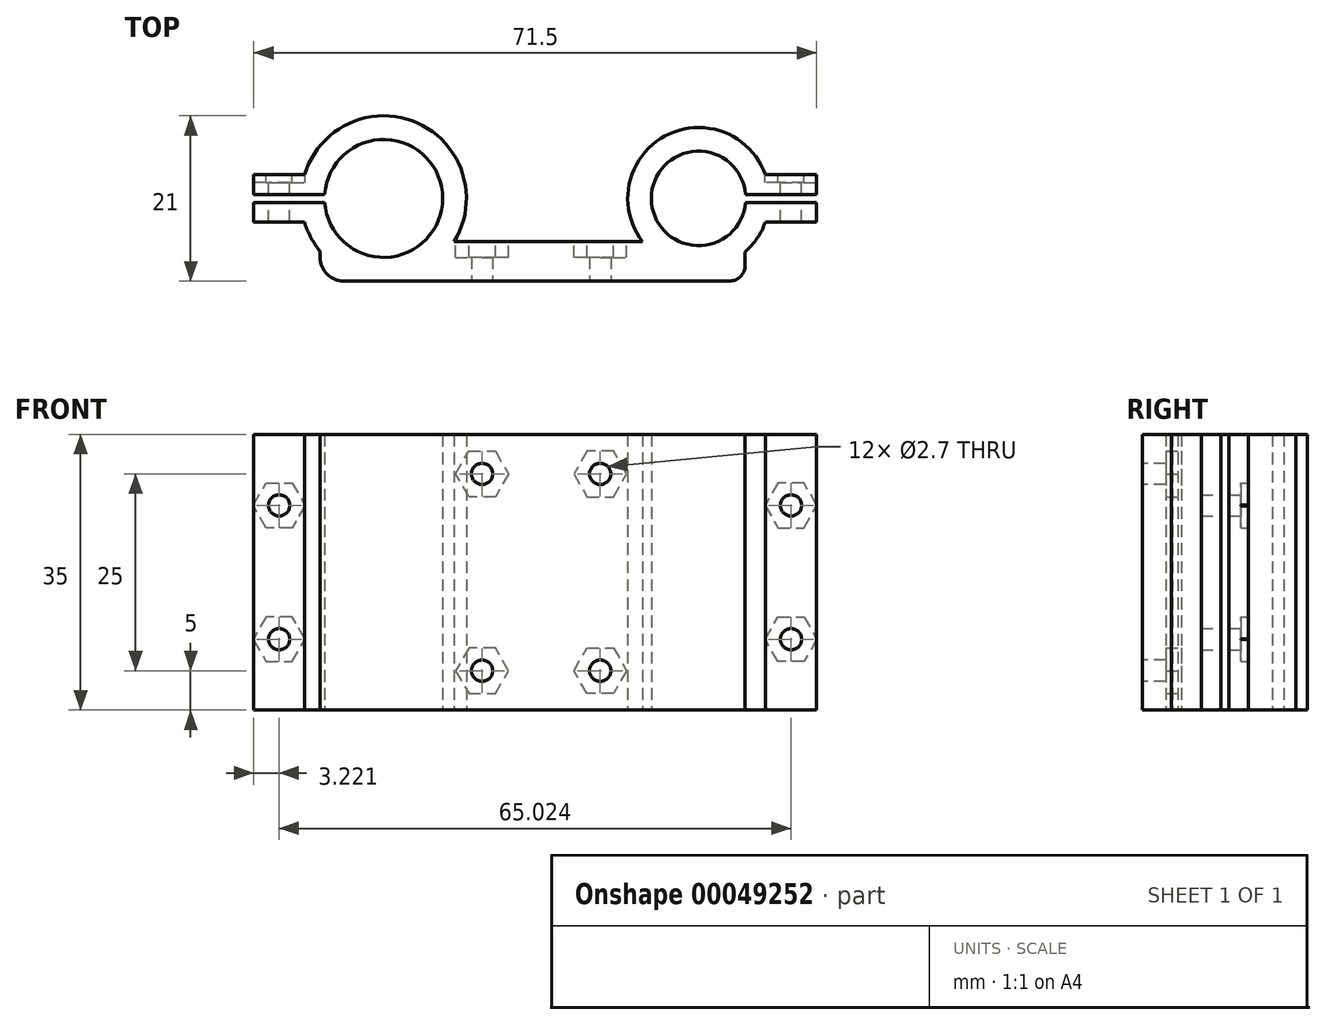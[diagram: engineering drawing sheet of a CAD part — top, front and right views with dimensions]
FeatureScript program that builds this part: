
annotation { "Feature Type Name" : "Feature", "Feature Type Description" : "" }
export const myFeature = defineFeature(function(context is Context, id is Id, definition is map)
    precondition{}
    {
        {
            var Q0;
            Q0=qCreatedBy(makeId("Top.planeOp"),FACE);
            var sketch = newSketch(context, id + "F0", { "sketchPlane" : qUnion([Q0])});
            skArc(sketch, "E0", {"start": v(-27.82, -25.7) * mm, "mid": v(-41.2, -21.15) * mm, "end": v(-42.53, -35.2) * mm});
            skArc(sketch, "E1", {"start": v(-30.33, -28.2) * mm, "mid": v(-42.3, -28.7) * mm, "end": v(-30.33, -29.2) * mm});
            skArc(sketch, "E2", {"start": v(-83.8, -29.2) * mm, "mid": v(-68.8, -28.7) * mm, "end": v(-83.8, -28.2) * mm});
            skArc(sketch, "E3", {"start": v(-86.37, -31.7) * mm, "mid": v(-85.57, -33.66) * mm, "end": v(-84.4, -35.4) * mm});
            skLineSegment(sketch, "E4", {"start": v(-42.53, -35.2) * mm, "end": v(-68.06, -35.2) * mm});
            skLineSegment(sketch, "E5", {"start": v(-84.4, -35.4) * mm, "end": v(-84.4, -36.2) * mm});
            skLineSegment(sketch, "E6", {"start": v(-81.4, -39.2) * mm, "end": v(-32.4, -39.2) * mm});
            skLineSegment(sketch, "E7", {"start": v(-30.4, -37.2) * mm, "end": v(-30.4, -35.5) * mm});
            skLineSegment(sketch, "E8", {"start": v(-76.3, -28.7) * mm, "end": v(-66.3, -28.7) * mm, "construction": true});
            skPoint(sketch, "E9", {"position": v(-56.3, -28.7) * mm});
            skLineSegment(sketch, "E10", {"start": v(-56.3, -28.7) * mm, "end": v(-51.3, -28.7) * mm, "construction": true});
            skLineSegment(sketch, "E11", {"start": v(-46.3, -28.7) * mm, "end": v(-36.3, -28.7) * mm, "construction": true});
            skLineSegment(sketch, "E12", {"start": v(-66.3, -28.7) * mm, "end": v(-61.3, -28.7) * mm, "construction": true});
            skLineSegment(sketch, "E13", {"start": v(-51.3, -28.7) * mm, "end": v(-46.3, -28.7) * mm, "construction": true});
            skLineSegment(sketch, "E14", {"start": v(-61.3, -28.7) * mm, "end": v(-56.3, -28.7) * mm, "construction": true});
            skPoint(sketch, "E15", {"position": v(-63.8, -28.7) * mm});
            skPoint(sketch, "E16", {"position": v(-48.8, -28.7) * mm});
            skPoint(sketch, "E17.visualSharp", {"position": v(-30.4, -39.2) * mm});
            skArc(sketch, "E17.filletArc", {"start": v(-32.4, -39.2) * mm, "mid": v(-30.98, -38.62) * mm, "end": v(-30.4, -37.2) * mm});
            skPoint(sketch, "E18", {"position": v(-76.3, -39.2) * mm});
            skLineSegment(sketch, "E19.rect.bottom", {"start": v(-92.8, -25.7) * mm, "end": v(-86.37, -25.7) * mm});
            skLineSegment(sketch, "E19.rect.top", {"start": v(-92.8, -31.7) * mm, "end": v(-86.37, -31.7) * mm});
            skLineSegment(sketch, "E19.rect.left", {"start": v(-92.8, -25.7) * mm, "end": v(-92.8, -28.2) * mm});
            skLineSegment(sketch, "E20.rect.right", {"start": v(-21.3, -25.7) * mm, "end": v(-21.3, -28.2) * mm});
            skLineSegment(sketch, "E21.rect.bottom", {"start": v(-92.8, -28.2) * mm, "end": v(-83.8, -28.2) * mm});
            skLineSegment(sketch, "E21.rect.top", {"start": v(-92.8, -29.2) * mm, "end": v(-83.8, -29.2) * mm});
            skPoint(sketch, "E22", {"position": v(-86.8, -29.2) * mm});
            skPoint(sketch, "E23", {"position": v(-86.8, -28.2) * mm});
            skPoint(sketch, "E24", {"position": v(-92.8, -28.2) * mm});
            skPoint(sketch, "E25", {"position": v(-92.8, -29.2) * mm});
            skPoint(sketch, "E26", {"position": v(-86.37, -25.7) * mm});
            skPoint(sketch, "E27", {"position": v(-86.37, -31.7) * mm});
            skPoint(sketch, "E28", {"position": v(-21.3, -28.2) * mm});
            skPoint(sketch, "E28.positionSnap0", {"position": v(-21.3, -28.7) * mm});
            skPoint(sketch, "E29", {"position": v(-21.3, -29.2) * mm});
            skPoint(sketch, "E30", {"position": v(-27.32, -28.2) * mm});
            skPoint(sketch, "E31", {"position": v(-27.32, -29.2) * mm});
            skPoint(sketch, "E32", {"position": v(-27.82, -31.7) * mm});
            skPoint(sketch, "E33", {"position": v(-31.11, -31.7) * mm});
            skPoint(sketch, "E34", {"position": v(-30.33, -28.2) * mm});
            skPoint(sketch, "E35", {"position": v(-27.82, -25.7) * mm});
            skPoint(sketch, "E21.rect.left.end.orphan", {"position": v(-94.34, -29.2) * mm});
            skPoint(sketch, "E21.rect.left.start.orphan", {"position": v(-94.34, -28.2) * mm});
            skLineSegment(sketch, "E36.trimOffspring", {"start": v(-92.8, -29.2) * mm, "end": v(-92.8, -31.7) * mm});
            skArc(sketch, "E37.trimOffspring", {"start": v(-68.06, -35.2) * mm, "mid": v(-71.47, -19.39) * mm, "end": v(-86.37, -25.7) * mm});
            skLineSegment(sketch, "E38.trimOffspring", {"start": v(-27.82, -31.7) * mm, "end": v(-21.3, -31.7) * mm});
            skLineSegment(sketch, "E39.trimOffspring", {"start": v(-30.33, -28.2) * mm, "end": v(-21.3, -28.2) * mm});
            skLineSegment(sketch, "E40.trimOffspring", {"start": v(-27.82, -25.7) * mm, "end": v(-21.3, -25.7) * mm});
            skPoint(sketch, "E41.orphan", {"position": v(-18.28, -28.2) * mm});
            skPoint(sketch, "E42.orphan", {"position": v(-18.28, -29.2) * mm});
            skLineSegment(sketch, "E43.trimOffspring", {"start": v(-21.3, -29.2) * mm, "end": v(-21.3, -31.7) * mm});
            skLineSegment(sketch, "E44.trimOffspring", {"start": v(-30.33, -29.2) * mm, "end": v(-21.3, -29.2) * mm});
            skPoint(sketch, "E45.visualSharp", {"position": v(-84.4, -39.2) * mm});
            skArc(sketch, "E45.filletArc", {"start": v(-84.4, -36.2) * mm, "mid": v(-83.51, -38.33) * mm, "end": v(-81.4, -39.2) * mm});
            skArc(sketch, "E46.trimOffspring", {"start": v(-30.4, -35.5) * mm, "mid": v(-28.87, -33.77) * mm, "end": v(-27.82, -31.7) * mm});
            skLineSegment(sketch, "E47", {"start": v(-56.3, -28.7) * mm, "end": v(-56.3, -39.2) * mm, "construction": true});
            skSolve(sketch);
        }
        {
            var Q0;
            Q0=makeQuery(id+"F0.imprint","IMPRINT",FACE,{"disambiguationData":[TD([[makeQuery(id+"F0.imprint","IMPRINT",EDGE,{"derivedFrom":sQuery(id+"F0.wireOp",EDGE,"E0")}),1.0]])]});
            var Q1;
            Q1 = qSketchRegion(id + "F2", true);
            extrude(context, id + "F1", {"entities" : qUnion([Q0, Q1]), "depth" : 35 * mm});
        }
        {
            var Q0;
            Q0=makeQuery(id+"F1.opExtrude","SWEPT_FACE",FACE,{"disambiguationData":[OSD([sQuery(id+"F0.wireOp",EDGE,"E6")])]});
            var sketch = newSketch(context, id + "F2", { "sketchPlane" : qUnion([Q0])});
            skLineSegment(sketch, "E48", {"start": v(-56.3, 35) * mm, "end": v(-56.3, 17.5) * mm, "construction": true});
            skLineSegment(sketch, "E49", {"start": v(-56.3, 17.5) * mm, "end": v(-81.4, 17.5) * mm, "construction": true});
            skLineSegment(sketch, "E50", {"start": v(-56.3, 17.5) * mm, "end": v(-32.4, 17.5) * mm, "construction": true});
            skPoint(sketch, "E51", {"position": v(139.68, 0) * mm});
            skPoint(sketch, "E52", {"position": v(-60.88, -141.08) * mm});
            skPoint(sketch, "E53.end.orphan", {"position": v(-63.8, 35) * mm});
            skLineSegment(sketch, "E54", {"start": v(-63.8, 30) * mm, "end": v(-63.8, 35) * mm});
            skPoint(sketch, "E55", {"position": v(-63.8, 30) * mm});
            skLineSegment(sketch, "E56.MirrorCS", {"start": v(-48.8, 30) * mm, "end": v(-48.8, 35) * mm});
            skLineSegment(sketch, "E57.MirrorCS", {"start": v(-56.3, 17.5) * mm, "end": v(-80.22, 17.5) * mm, "construction": true});
            skLineSegment(sketch, "E58.MirrorCS", {"start": v(-48.8, 5) * mm, "end": v(-48.8, 0) * mm});
            skLineSegment(sketch, "E59.MirrorCS", {"start": v(-63.8, 5) * mm, "end": v(-63.8, 0) * mm});
            skPoint(sketch, "E60", {"position": v(-48.8, 30) * mm});
            skPoint(sketch, "E61", {"position": v(-48.8, 5) * mm});
            skPoint(sketch, "E62", {"position": v(-63.8, 5) * mm});
            skCircle(sketch, "E63.cCircle", {"center": v(-48.8, 30) * mm, "radius": 2.85 * mm, "construction": true});
            skLineSegment(sketch, "E63.0", {"start": v(-45.96, 31.65) * mm, "end": v(-45.96, 28.35) * mm});
            skLineSegment(sketch, "E63.1", {"start": v(-45.96, 28.35) * mm, "end": v(-48.8, 26.7) * mm});
            skLineSegment(sketch, "E63.2", {"start": v(-48.8, 26.7) * mm, "end": v(-51.66, 28.35) * mm});
            skLineSegment(sketch, "E63.3", {"start": v(-51.66, 28.35) * mm, "end": v(-51.66, 31.65) * mm});
            skLineSegment(sketch, "E63.4", {"start": v(-51.66, 31.65) * mm, "end": v(-48.8, 33.3) * mm});
            skLineSegment(sketch, "E63.5", {"start": v(-48.8, 33.3) * mm, "end": v(-45.96, 31.65) * mm});
            skPoint(sketch, "E63.0.midPoint", {"position": v(-45.96, 30) * mm});
            skLineSegment(sketch, "E64.MirrorCS", {"start": v(-35.6, 17.5) * mm, "end": v(-59.52, 17.5) * mm, "construction": true});
            skCircle(sketch, "E65.MirrorC", {"center": v(-48.8, 5) * mm, "radius": 2.85 * mm, "construction": true});
            skLineSegment(sketch, "E66.MirrorCS", {"start": v(-45.96, 3.35) * mm, "end": v(-45.96, 6.65) * mm});
            skLineSegment(sketch, "E67.MirrorCS", {"start": v(-48.8, 1.7) * mm, "end": v(-45.96, 3.35) * mm});
            skLineSegment(sketch, "E68.MirrorCS", {"start": v(-48.8, 8.3) * mm, "end": v(-51.66, 6.65) * mm});
            skPoint(sketch, "E69.MirrorP", {"position": v(-45.96, 5) * mm});
            skLineSegment(sketch, "E70.MirrorCS", {"start": v(-51.66, 3.35) * mm, "end": v(-48.8, 1.7) * mm});
            skLineSegment(sketch, "E71.MirrorCS", {"start": v(-51.66, 6.65) * mm, "end": v(-51.66, 3.35) * mm});
            skLineSegment(sketch, "E72.MirrorCS", {"start": v(-45.96, 6.65) * mm, "end": v(-48.8, 8.3) * mm});
            skLineSegment(sketch, "E73.MirrorCS", {"start": v(-66.66, 31.65) * mm, "end": v(-66.66, 28.35) * mm});
            skPoint(sketch, "E74.MirrorP", {"position": v(-66.66, 30) * mm});
            skCircle(sketch, "E75.MirrorC", {"center": v(-63.8, 30) * mm, "radius": 2.85 * mm, "construction": true});
            skLineSegment(sketch, "E76.MirrorCS", {"start": v(-66.66, 28.35) * mm, "end": v(-63.8, 26.7) * mm});
            skLineSegment(sketch, "E77.MirrorCS", {"start": v(-63.8, 26.7) * mm, "end": v(-60.96, 28.35) * mm});
            skLineSegment(sketch, "E78.MirrorCS", {"start": v(-60.96, 28.35) * mm, "end": v(-60.96, 31.65) * mm});
            skLineSegment(sketch, "E79.MirrorCS", {"start": v(-60.96, 31.65) * mm, "end": v(-63.8, 33.3) * mm});
            skLineSegment(sketch, "E80.MirrorCS", {"start": v(-63.8, 33.3) * mm, "end": v(-66.66, 31.65) * mm});
            skLineSegment(sketch, "E81.MirrorCS", {"start": v(-66.66, 3.35) * mm, "end": v(-66.66, 6.65) * mm});
            skPoint(sketch, "E82.MirrorP", {"position": v(-66.66, 5) * mm});
            skLineSegment(sketch, "E83.MirrorCS", {"start": v(-63.8, 8.3) * mm, "end": v(-60.96, 6.65) * mm});
            skLineSegment(sketch, "E84.MirrorCS", {"start": v(-60.96, 6.65) * mm, "end": v(-60.96, 3.35) * mm});
            skCircle(sketch, "E85.MirrorC", {"center": v(-63.8, 5) * mm, "radius": 2.85 * mm, "construction": true});
            skLineSegment(sketch, "E86.MirrorCS", {"start": v(-60.96, 3.35) * mm, "end": v(-63.8, 1.7) * mm});
            skLineSegment(sketch, "E87.MirrorCS", {"start": v(-66.66, 6.65) * mm, "end": v(-63.8, 8.3) * mm});
            skLineSegment(sketch, "E88.MirrorCS", {"start": v(-63.8, 1.7) * mm, "end": v(-66.66, 3.35) * mm});
            skCircle(sketch, "E89.MirrorC", {"center": v(-64.88, 27.43) * mm, "radius": 2.85 * mm, "construction": true});
            skSolve(sketch);
        }
        {
            var Q0;
            Q0=sQuery(id+"F2.wireOp",VERTEX,"E55");
            var Q1;
            Q1=sQuery(id+"F2.wireOp",VERTEX,"E60");
            var Q2;
            Q2=sQuery(id+"F2.wireOp",VERTEX,"E61");
            var Q3;
            Q3=sQuery(id+"F2.wireOp",VERTEX,"E62");
            var Q4;
            Q4=makeQuery(id+"F1.opExtrude","SWEPT_BODY",BODY,{"disambiguationData":[OSD([sQuery(id+"F0.wireOp",EDGE,"E0"),sQuery(id+"F0.wireOp",EDGE,"E1"),sQuery(id+"F0.wireOp",EDGE,"E2"),sQuery(id+"F0.wireOp",EDGE,"E3"),sQuery(id+"F0.wireOp",EDGE,"E4"),sQuery(id+"F0.wireOp",EDGE,"E5"),sQuery(id+"F0.wireOp",EDGE,"E6"),sQuery(id+"F0.wireOp",EDGE,"E7"),sQuery(id+"F0.wireOp",EDGE,"E17.filletArc"),sQuery(id+"F0.wireOp",EDGE,"E19.rect.bottom"),sQuery(id+"F0.wireOp",EDGE,"E19.rect.top"),sQuery(id+"F0.wireOp",EDGE,"E19.rect.left"),sQuery(id+"F0.wireOp",EDGE,"E20.rect.right"),sQuery(id+"F0.wireOp",EDGE,"E21.rect.bottom"),sQuery(id+"F0.wireOp",EDGE,"E21.rect.top"),sQuery(id+"F0.wireOp",EDGE,"E36.trimOffspring"),sQuery(id+"F0.wireOp",EDGE,"E37.trimOffspring"),sQuery(id+"F0.wireOp",EDGE,"E38.trimOffspring"),sQuery(id+"F0.wireOp",EDGE,"E39.trimOffspring"),sQuery(id+"F0.wireOp",EDGE,"E40.trimOffspring"),sQuery(id+"F0.wireOp",EDGE,"E43.trimOffspring"),sQuery(id+"F0.wireOp",EDGE,"E44.trimOffspring"),sQuery(id+"F0.wireOp",EDGE,"E45.filletArc"),sQuery(id+"F0.wireOp",EDGE,"E46.trimOffspring")])]});
            hole(context, id + "F3", {"style" : HoleStyle.SIMPLE, "holeDiameter" : 2.7 * mm, "endStyle" : HoleEndStyle.THROUGH, "locations" : qUnion([Q0, Q1, Q2, Q3]), "scope" : qUnion([Q4])});
        }
        {
            var Q0;
            Q0=makeQuery(id+"F1.opExtrude","SWEPT_FACE",FACE,{"disambiguationData":[OSD([sQuery(id+"F0.wireOp",EDGE,"E4")])]});
            var sketch = newSketch(context, id + "F4", { "sketchPlane" : qUnion([Q0])});
            skCircle(sketch, "E90.cCircle", {"center": v(48.8, 30) * mm, "radius": 2.9 * mm, "construction": true});
            skLineSegment(sketch, "E90.0", {"start": v(52.16, 30) * mm, "end": v(50.48, 27.1) * mm});
            skLineSegment(sketch, "E90.1", {"start": v(50.48, 27.1) * mm, "end": v(47.13, 27.1) * mm});
            skLineSegment(sketch, "E90.2", {"start": v(47.13, 27.1) * mm, "end": v(45.46, 30) * mm});
            skLineSegment(sketch, "E90.3", {"start": v(45.46, 30) * mm, "end": v(47.13, 32.9) * mm});
            skLineSegment(sketch, "E90.4", {"start": v(47.13, 32.9) * mm, "end": v(50.48, 32.9) * mm});
            skLineSegment(sketch, "E90.5", {"start": v(50.48, 32.9) * mm, "end": v(52.16, 30) * mm});
            skPoint(sketch, "E90.0.midPoint", {"position": v(51.32, 28.55) * mm});
            skPoint(sketch, "E91", {"position": v(55.3, 17.5) * mm});
            skLineSegment(sketch, "E92", {"start": v(55.3, 17.5) * mm, "end": v(65.53, 17.5) * mm});
            skCircle(sketch, "E93.MirrorC", {"center": v(48.8, 5) * mm, "radius": 2.9 * mm, "construction": true});
            skLineSegment(sketch, "E94.MirrorCS", {"start": v(50.48, 7.9) * mm, "end": v(47.13, 7.9) * mm});
            skLineSegment(sketch, "E95.MirrorCS", {"start": v(47.13, 2.1) * mm, "end": v(50.48, 2.1) * mm});
            skLineSegment(sketch, "E96.MirrorCS", {"start": v(45.46, 5) * mm, "end": v(47.13, 2.1) * mm});
            skLineSegment(sketch, "E97.MirrorCS", {"start": v(50.48, 2.1) * mm, "end": v(52.16, 5) * mm});
            skLineSegment(sketch, "E98.MirrorCS", {"start": v(52.16, 5) * mm, "end": v(50.48, 7.9) * mm});
            skPoint(sketch, "E99.MirrorP", {"position": v(51.32, 6.45) * mm});
            skLineSegment(sketch, "E100.MirrorCS", {"start": v(47.13, 7.9) * mm, "end": v(45.46, 5) * mm});
            skLineSegment(sketch, "E101", {"start": v(48.8, 30) * mm, "end": v(63.8, 30) * mm});
            skPoint(sketch, "E102", {"position": v(56.3, 30) * mm});
            skLineSegment(sketch, "E103", {"start": v(56.3, 30) * mm, "end": v(56.3, 17.5) * mm});
            skLineSegment(sketch, "E104.MirrorCS", {"start": v(67.16, 30) * mm, "end": v(65.48, 32.9) * mm});
            skCircle(sketch, "E105.MirrorC", {"center": v(63.8, 30) * mm, "radius": 2.9 * mm, "construction": true});
            skLineSegment(sketch, "E106.MirrorCS", {"start": v(62.13, 32.9) * mm, "end": v(60.46, 30) * mm});
            skLineSegment(sketch, "E107.MirrorCS", {"start": v(60.46, 30) * mm, "end": v(62.13, 27.1) * mm});
            skLineSegment(sketch, "E108.MirrorCS", {"start": v(63.8, 30) * mm, "end": v(48.8, 30) * mm});
            skLineSegment(sketch, "E109.MirrorCS", {"start": v(65.48, 32.9) * mm, "end": v(62.13, 32.9) * mm});
            skPoint(sketch, "E110.MirrorP", {"position": v(61.3, 28.55) * mm});
            skLineSegment(sketch, "E111.MirrorCS", {"start": v(62.13, 27.1) * mm, "end": v(65.48, 27.1) * mm});
            skLineSegment(sketch, "E112.MirrorCS", {"start": v(65.48, 27.1) * mm, "end": v(67.16, 30) * mm});
            skLineSegment(sketch, "E113.MirrorCS", {"start": v(65.48, 2.1) * mm, "end": v(62.13, 2.1) * mm});
            skLineSegment(sketch, "E114.MirrorCS", {"start": v(62.13, 7.9) * mm, "end": v(65.48, 7.9) * mm});
            skLineSegment(sketch, "E115.MirrorCS", {"start": v(62.13, 2.1) * mm, "end": v(60.46, 5) * mm});
            skCircle(sketch, "E116.MirrorC", {"center": v(63.8, 5) * mm, "radius": 2.9 * mm, "construction": true});
            skLineSegment(sketch, "E117.MirrorCS", {"start": v(67.16, 5) * mm, "end": v(65.48, 2.1) * mm});
            skLineSegment(sketch, "E118.MirrorCS", {"start": v(65.48, 7.9) * mm, "end": v(67.16, 5) * mm});
            skPoint(sketch, "E119.MirrorP", {"position": v(61.3, 6.45) * mm});
            skLineSegment(sketch, "E120.MirrorCS", {"start": v(60.46, 5) * mm, "end": v(62.13, 7.9) * mm});
            skSolve(sketch);
        }
        {
            var Q0;
            Q0 = qSketchRegion(id + "F4", true);
            extrude(context, id + "F5", {"entities" : qUnion([Q0]), "operationType" : NewBodyOperationType.REMOVE, "oppositeDirection" : true, "depth" : 1 * mm});
        }
        {
            var Q0;
            Q0=makeQuery(id+"F1.opExtrude","SWEPT_FACE",FACE,{"disambiguationData":[OSD([sQuery(id+"F0.wireOp",EDGE,"E4")])]});
            extrude(context, id + "F6", {"entities" : qUnion([Q0]), "operationType" : NewBodyOperationType.ADD, "depth" : 1 * mm});
        }
        {
            var Q0;
            Q0=makeQuery(id+"F1.opExtrude","SWEPT_FACE",FACE,{"disambiguationData":[OSD([sQuery(id+"F0.wireOp",EDGE,"E19.rect.bottom")])]});
            var sketch = newSketch(context, id + "F7", { "sketchPlane" : qUnion([Q0])});
            skPoint(sketch, "E121", {"position": v(89.59, 35) * mm});
            skPoint(sketch, "E122", {"position": v(91.36, 17.5) * mm});
            skPoint(sketch, "E123", {"position": v(89.59, 17.5) * mm});
            skPoint(sketch, "E124", {"position": v(89.59, 26) * mm});
            skPoint(sketch, "E125", {"position": v(89.59, 9) * mm});
            skCircle(sketch, "E126.cCircle", {"center": v(89.59, 9) * mm, "radius": 2.85 * mm, "construction": true});
            skLineSegment(sketch, "E126.0", {"start": v(92.88, 9) * mm, "end": v(91.23, 6.15) * mm});
            skLineSegment(sketch, "E126.1", {"start": v(91.23, 6.15) * mm, "end": v(87.94, 6.15) * mm});
            skLineSegment(sketch, "E126.2", {"start": v(87.94, 6.15) * mm, "end": v(86.3, 9) * mm});
            skLineSegment(sketch, "E126.3", {"start": v(86.3, 9) * mm, "end": v(87.94, 11.85) * mm});
            skLineSegment(sketch, "E126.4", {"start": v(87.94, 11.85) * mm, "end": v(91.23, 11.85) * mm});
            skLineSegment(sketch, "E126.5", {"start": v(91.23, 11.85) * mm, "end": v(92.88, 9) * mm});
            skPoint(sketch, "E126.0.midPoint", {"position": v(92.06, 7.58) * mm});
            skLineSegment(sketch, "E127", {"start": v(91.36, 17.5) * mm, "end": v(89.59, 17.5) * mm, "construction": true});
            skLineSegment(sketch, "E128.MirrorCS", {"start": v(91.23, 28.85) * mm, "end": v(87.94, 28.85) * mm});
            skLineSegment(sketch, "E129.MirrorCS", {"start": v(92.88, 26) * mm, "end": v(91.23, 28.85) * mm});
            skCircle(sketch, "E130.MirrorC", {"center": v(89.59, 26) * mm, "radius": 2.85 * mm, "construction": true});
            skLineSegment(sketch, "E131.MirrorCS", {"start": v(87.94, 28.85) * mm, "end": v(86.3, 26) * mm});
            skLineSegment(sketch, "E132.MirrorCS", {"start": v(87.94, 23.15) * mm, "end": v(91.23, 23.15) * mm});
            skLineSegment(sketch, "E133.MirrorCS", {"start": v(86.3, 26) * mm, "end": v(87.94, 23.15) * mm});
            skLineSegment(sketch, "E134.MirrorCS", {"start": v(91.23, 23.15) * mm, "end": v(92.88, 26) * mm});
            skPoint(sketch, "E135.MirrorP", {"position": v(92.06, 27.42) * mm});
            skPoint(sketch, "E136.start.orphan", {"position": v(91.36, 26) * mm});
            skPoint(sketch, "E137.start.orphan", {"position": v(91.36, 9) * mm});
            skPoint(sketch, "E138.trimOffspring.end.orphan", {"position": v(89.59, 0) * mm});
            skSolve(sketch);
        }
        {
            var Q0;
            Q0=makeQuery(id+"F1.opExtrude","SWEPT_FACE",FACE,{"disambiguationData":[OSD([sQuery(id+"F0.wireOp",EDGE,"E40.trimOffspring")])]});
            var sketch = newSketch(context, id + "F8", { "sketchPlane" : qUnion([Q0])});
            skPoint(sketch, "E139", {"position": v(24.56, 35) * mm});
            skPoint(sketch, "E140", {"position": v(24.56, 0) * mm});
            skLineSegment(sketch, "E141", {"start": v(24.56, 35) * mm, "end": v(24.56, 0) * mm});
            skPoint(sketch, "E142", {"position": v(24.56, 17.5) * mm});
            skPoint(sketch, "E143", {"position": v(26.19, 17.5) * mm});
            skLineSegment(sketch, "E144", {"start": v(24.56, 17.5) * mm, "end": v(27.82, 17.5) * mm});
            skLineSegment(sketch, "E145", {"start": v(26.19, 11.85) * mm, "end": v(26.19, 9) * mm});
            skLineSegment(sketch, "E146.MirrorCS", {"start": v(26.19, 23.15) * mm, "end": v(26.19, 26) * mm});
            skLineSegment(sketch, "E147", {"start": v(26.19, 26) * mm, "end": v(22.2, 26) * mm});
            skLineSegment(sketch, "E148", {"start": v(26.19, 9) * mm, "end": v(22.28, 9) * mm});
            skPoint(sketch, "E149", {"position": v(24.56, 26) * mm});
            skPoint(sketch, "E150", {"position": v(24.56, 9) * mm});
            skCircle(sketch, "E151.cCircle", {"center": v(24.56, 26) * mm, "radius": 2.85 * mm, "construction": true});
            skLineSegment(sketch, "E151.0", {"start": v(27.86, 26) * mm, "end": v(26.21, 23.15) * mm});
            skLineSegment(sketch, "E151.1", {"start": v(26.21, 23.15) * mm, "end": v(22.92, 23.15) * mm});
            skLineSegment(sketch, "E151.2", {"start": v(22.92, 23.15) * mm, "end": v(21.27, 26) * mm});
            skLineSegment(sketch, "E151.3", {"start": v(21.27, 26) * mm, "end": v(22.92, 28.85) * mm});
            skLineSegment(sketch, "E151.4", {"start": v(22.92, 28.85) * mm, "end": v(26.21, 28.85) * mm});
            skLineSegment(sketch, "E151.5", {"start": v(26.21, 28.85) * mm, "end": v(27.86, 26) * mm});
            skPoint(sketch, "E151.0.midPoint", {"position": v(27.03, 24.57) * mm});
            skLineSegment(sketch, "E152.MirrorCS", {"start": v(27.86, 9) * mm, "end": v(26.21, 11.85) * mm});
            skLineSegment(sketch, "E153.MirrorCS", {"start": v(26.21, 11.85) * mm, "end": v(22.92, 11.85) * mm});
            skLineSegment(sketch, "E154.MirrorCS", {"start": v(26.21, 6.15) * mm, "end": v(27.86, 9) * mm});
            skLineSegment(sketch, "E155.MirrorCS", {"start": v(22.92, 11.85) * mm, "end": v(21.27, 9) * mm});
            skPoint(sketch, "E156.MirrorP", {"position": v(27.03, 10.43) * mm});
            skLineSegment(sketch, "E157.MirrorCS", {"start": v(26.19, 9) * mm, "end": v(22.2, 9) * mm});
            skLineSegment(sketch, "E158.MirrorCS", {"start": v(22.92, 6.15) * mm, "end": v(26.21, 6.15) * mm});
            skLineSegment(sketch, "E159.MirrorCS", {"start": v(21.27, 9) * mm, "end": v(22.92, 6.15) * mm});
            skSolve(sketch);
        }
        {
            var Q0;
            Q0=sQuery(id+"F8.wireOp",VERTEX,"E149");
            var Q1;
            Q1=sQuery(id+"F8.wireOp",VERTEX,"E150");
            var Q2;
            Q2=sQuery(id+"F7.wireOp",VERTEX,"E125");
            var Q3;
            Q3=sQuery(id+"F7.wireOp",VERTEX,"E124");
            var Q4;
            Q4=makeQuery(id+"F1.opExtrude","SWEPT_BODY",BODY,{"disambiguationData":[OSD([sQuery(id+"F0.wireOp",EDGE,"E0"),sQuery(id+"F0.wireOp",EDGE,"E1"),sQuery(id+"F0.wireOp",EDGE,"E2"),sQuery(id+"F0.wireOp",EDGE,"E3"),sQuery(id+"F0.wireOp",EDGE,"E4"),sQuery(id+"F0.wireOp",EDGE,"E5"),sQuery(id+"F0.wireOp",EDGE,"E6"),sQuery(id+"F0.wireOp",EDGE,"E7"),sQuery(id+"F0.wireOp",EDGE,"E17.filletArc"),sQuery(id+"F0.wireOp",EDGE,"E19.rect.bottom"),sQuery(id+"F0.wireOp",EDGE,"E19.rect.top"),sQuery(id+"F0.wireOp",EDGE,"E19.rect.left"),sQuery(id+"F0.wireOp",EDGE,"E20.rect.right"),sQuery(id+"F0.wireOp",EDGE,"E21.rect.bottom"),sQuery(id+"F0.wireOp",EDGE,"E21.rect.top"),sQuery(id+"F0.wireOp",EDGE,"E36.trimOffspring"),sQuery(id+"F0.wireOp",EDGE,"E37.trimOffspring"),sQuery(id+"F0.wireOp",EDGE,"E38.trimOffspring"),sQuery(id+"F0.wireOp",EDGE,"E39.trimOffspring"),sQuery(id+"F0.wireOp",EDGE,"E40.trimOffspring"),sQuery(id+"F0.wireOp",EDGE,"E43.trimOffspring"),sQuery(id+"F0.wireOp",EDGE,"E44.trimOffspring"),sQuery(id+"F0.wireOp",EDGE,"E45.filletArc"),sQuery(id+"F0.wireOp",EDGE,"E46.trimOffspring")])]});
            hole(context, id + "F9", {"style" : HoleStyle.SIMPLE, "holeDiameter" : 2.7 * mm, "endStyle" : HoleEndStyle.THROUGH, "locations" : qUnion([Q0, Q1, Q2, Q3]), "scope" : qUnion([Q4])});
        }
        {
            var Q0;
            Q0 = qSketchRegion(id + "F8", true);
            extrude(context, id + "F10", {"entities" : qUnion([Q0]), "operationType" : NewBodyOperationType.REMOVE, "oppositeDirection" : true, "depth" : 1 * mm});
        }
        {
            var Q0;
            Q0 = qSketchRegion(id + "F7", true);
            extrude(context, id + "F11", {"entities" : qUnion([Q0]), "operationType" : NewBodyOperationType.REMOVE, "oppositeDirection" : true, "depth" : 1 * mm});
        }
    });
